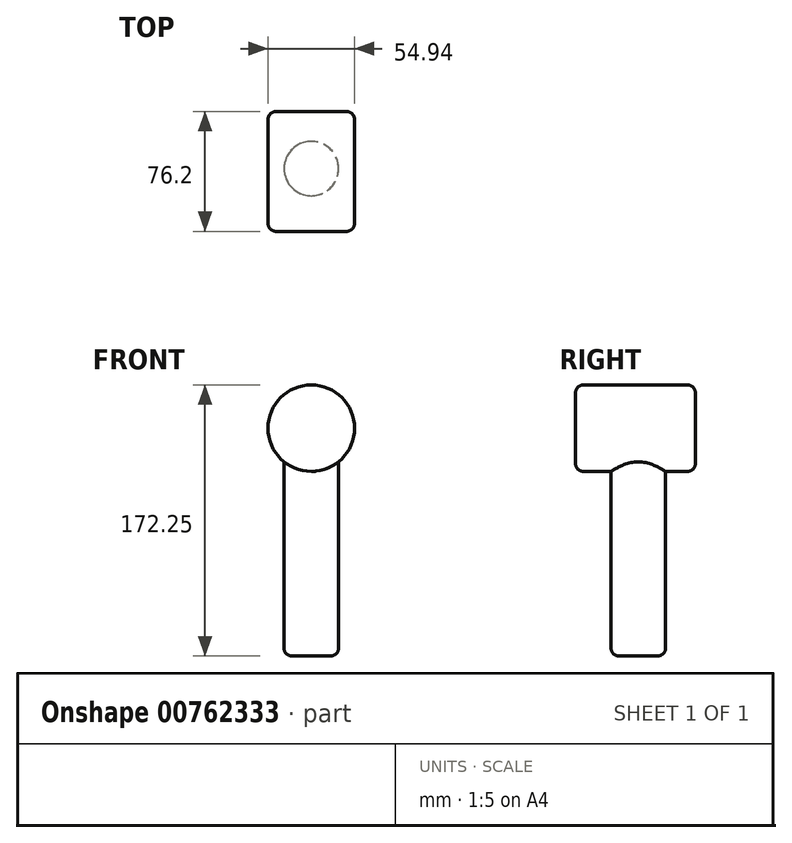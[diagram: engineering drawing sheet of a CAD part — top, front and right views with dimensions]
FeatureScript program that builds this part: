
annotation { "Feature Type Name" : "Feature", "Feature Type Description" : "" }
export const myFeature = defineFeature(function(context is Context, id is Id, definition is map)
    precondition{}
    {
        {
            var Q0;
            Q0=qCreatedBy(makeId("Front.planeOp"),FACE);
            var sketch = newSketch(context, id + "F0", { "sketchPlane" : qUnion([Q0])});
            skCircle(sketch, "E0", {"center": v(0, 0) * mm, "radius": 27.47 * mm});
            skSolve(sketch);
        }
        {
            var Q0;
            Q0=makeQuery(id+"F0.imprint","IMPRINT",FACE,{"disambiguationData":[TD([[makeQuery(id+"F0.imprint","IMPRINT",EDGE,{"derivedFrom":sQuery(id+"F0.wireOp",EDGE,"E0")}),1.0]])]});
            extrude(context, id + "F1", {"entities" : qUnion([Q0]), "depth" : 76.2 * mm, "offsetDistance" : 25.4 * mm});
        }
        {
            var Q0;
            Q0=qCreatedBy(makeId("Top.planeOp"),FACE);
            var sketch = newSketch(context, id + "F2", { "sketchPlane" : qUnion([Q0])});
            skCircle(sketch, "E1", {"center": v(0, -36.28) * mm, "radius": 17.3 * mm});
            skSolve(sketch);
        }
        {
            var Q0;
            Q0 = qSketchRegion(id + "F2", true);
            extrude(context, id + "F3", {"entities" : qUnion([Q0]), "operationType" : NewBodyOperationType.ADD, "oppositeDirection" : true, "depth" : 144.78 * mm, "offsetDistance" : 25.4 * mm});
        }
        {
            var Q0;
            Q0=makeQuery(id+"F3.opExtrude","CAP_FACE",FACE,{"disambiguationData":[OSD([sQuery(id+"F2.wireOp",EDGE,"E1")])],"isStart":false});
            fillet(context, id + "F4", {"entities" : qUnion([Q0]), "radius" : 5.08 * mm, "tangentPropagation" : true, "allowEdgeOverflow" : false});
        }
        {
            var Q0;
            Q0=makeQuery(id+"F1.opExtrude","CAP_EDGE",EDGE,{"disambiguationData":[OSD([sQuery(id+"F0.wireOp",EDGE,"E0")])],"isStart":true});
            fillet(context, id + "F5", {"entities" : qUnion([Q0]), "radius" : 5.08 * mm, "tangentPropagation" : true, "allowEdgeOverflow" : false});
        }
        {
            var Q0;
            Q0=makeQuery(id+"F1.opExtrude","CAP_FACE",FACE,{"disambiguationData":[OSD([sQuery(id+"F0.wireOp",EDGE,"E0")])],"isStart":false});
            fillet(context, id + "F6", {"entities" : qUnion([Q0]), "radius" : 5.08 * mm, "tangentPropagation" : true, "allowEdgeOverflow" : false});
        }
    });
